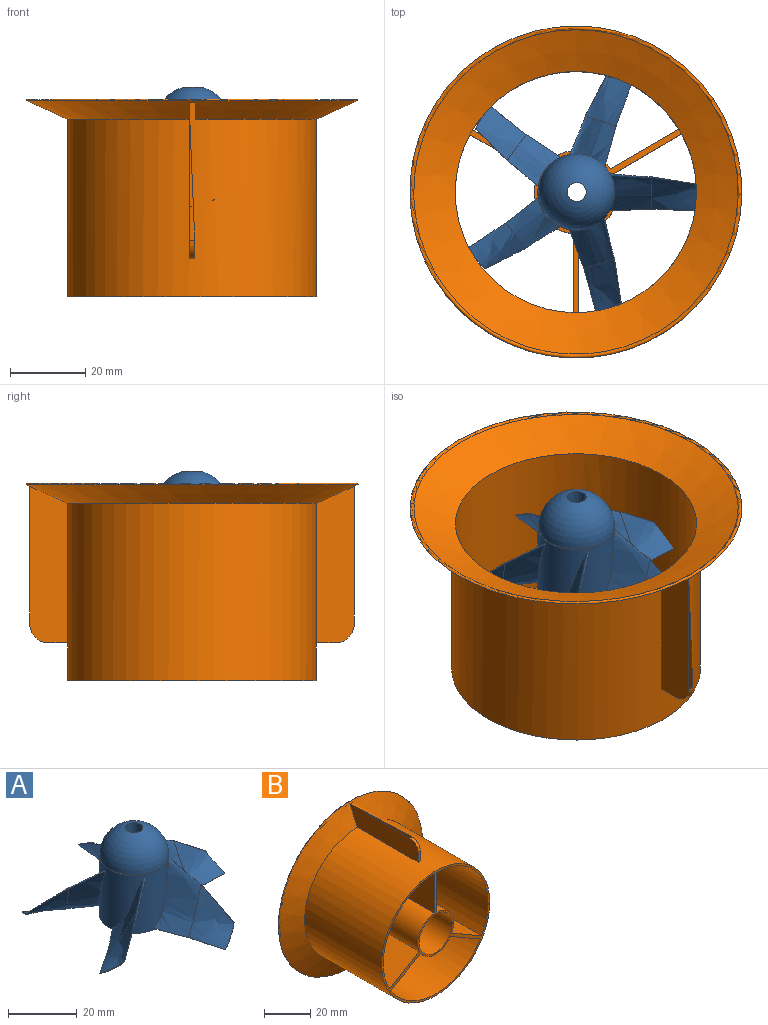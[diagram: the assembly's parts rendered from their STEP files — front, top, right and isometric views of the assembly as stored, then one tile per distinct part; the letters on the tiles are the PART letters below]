
ASSEMBLY  parts=2 mates=1
PART A: 38 faces, bbox 61.4x63.6x30.5 mm
  f0: bspline ~19.39x13.51mm, area 431mm2, adj f1,f36
  f1: cylinder r=10.1mm len=20.7mm, axis (0,0,-1), area 1234.5mm2, adj f0,f2,f5,f8,f11,f31,f32,f33
  f2: bspline ~19.22x14.14mm, area 417.3mm2, adj f1,f3
  f3: bspline ~14.62x13.87mm, area 306mm2, adj f2,f4
  f4: cylinder r=32mm len=6.27mm, axis (0,0,-1), area 2.2mm2, adj f3
  f5: bspline ~19.13x14.23mm, area 410.5mm2, adj f1,f6
  f6: bspline ~15.36x13.41mm, area 306mm2, adj f5,f7
  f7: cylinder r=32mm len=5.31mm, axis (0,0,-1), area 2.2mm2, adj f6
  f8: bspline ~19.4x11.33mm, area 432.5mm2, adj f1,f9
  f9: bspline ~13.41x12.41mm, area 306mm2, adj f8,f10
  f10: cylinder r=32mm len=7.16mm, axis (0,0,-1), area 2.2mm2, adj f9
  f11: plane 20.2x20.2mm, normal (0,0,-1), area 60.3mm2, adj f1,f12
  f12: cylinder r=9.1mm len=20.7mm, axis (0,0,-1), area 1183.5mm2, adj f11,f13,f14,f15,f16,f18,f19,f21
  f13: plane 0.06x0.02mm, normal (-1,0,0), area 0mm2, adj f12,f14,f15
  f14: bspline ~12.5x0.96mm, area 0mm2, adj f12,f13,f15
  f15: plane 0.06x0.04mm, normal (0,0,1), area 0mm2, adj f12,f13,f14
  f16: plane 0.32x0.21mm, normal (0,0,1), area 0mm2, adj f12,f17,f18
  f17: plane 0.1x0.03mm, normal (-0.31,0.95,0), area 0mm2, adj f16,f18
  f18: bspline ~0.35x0.21mm, area 0mm2, adj f12,f16,f17
  f19: plane 0.37x0.25mm, normal (0,0,1), area 0mm2, adj f12,f20,f21
  f20: plane 0.08x0.06mm, normal (0.81,-0.59,0), area 0mm2, adj f19,f21
  f21: bspline ~0.37x0.29mm, area 0mm2, adj f12,f19,f20
  f22: bspline ~0.49x0.42mm, area 0.1mm2, adj f12,f23,f24
  f23: plane 0.08x0.06mm, normal (0.81,0.59,0), area 0mm2, adj f22,f24
  f24: plane 0.44x0.42mm, normal (0,0,1), area 0.1mm2, adj f12,f22,f23
  f25: plane 0.08x0.03mm, normal (-0.31,-0.95,0), area 0mm2, adj f12,f26,f27
  f26: bspline ~12.19x3.98mm, area 0mm2, adj f12,f25,f27
  f27: plane 0.08x0.08mm, normal (0,0,1), area 0mm2, adj f12,f25,f26
  f28: plane 18.2x18.2mm, normal (0,0,-1), area 240.5mm2, adj f12,f29
  f29: cylinder r=2.5mm len=9.79mm, axis (0,0,-1), area 153.7mm2, adj f28,f30
  f30: sphere r=10.1mm, area 621mm2, adj f29,f31,f32
  f31: plane 20.2x10.21mm, normal (0,0,-1), area 4.6mm2, adj f1,f30
  f32: plane 20.2x10.21mm, normal (0,0,1), area 4.6mm2, adj f1,f30
  f33: bspline ~19.34x13.62mm, area 17.7mm2, adj f1,f34
  f34: bspline ~14.6x13.41mm, area 306mm2, adj f33,f35
  f35: cylinder r=32mm len=6.55mm, axis (0,0,-1), area 2.2mm2, adj f34
  f36: bspline ~13.82x13.41mm, area 306mm2, adj f0,f37
  f37: cylinder r=32mm len=7.06mm, axis (0,0,-1), area 2.2mm2, adj f36
PART B: 27 faces, bbox 95.3x52.4x95.3 mm
  f0: cylinder r=32mm len=64mm, axis (0,-1,0), area 9343.6mm2, adj f7,f8,f16,f17,f19,f20,f22,f23
  f1: plane 41.54x10.02mm, normal (-1,0,0), area 387.9mm2, adj f2,f5,f6,f10,f15
  f2: cylinder r=43mm len=36.54mm, axis (0,-1,0), area 54.8mm2, adj f1,f3,f5,f15
  f3: plane 41.54x10.02mm, normal (1,0,0), area 387.9mm2, adj f2,f5,f6,f10,f15
  f4: cylinder r=43mm len=36.55mm, axis (0,-1,0), area 54.8mm2, adj f5,f11,f12,f14
  f5: cone r=33mm half-angle=65.6deg, axis (0,1,0), area 2896.4mm2, adj f1,f2,f3,f4,f6,f9,f11,f12
  f6: cylinder r=33mm len=66mm, axis (0,-1,0), area 9634.2mm2, adj f1,f3,f5,f7,f10,f11,f12,f13
  f7: plane 66x66mm, normal (0,-1,0), area 360.1mm2, adj f0,f6,f16,f17,f18,f19,f20,f21
  f8: cone r=31.99mm half-angle=65.6deg, axis (0,1,0), area 2852.7mm2, adj f0,f9
  f9: torus R=43.52mm, axis (0,-1,0), area 371.9mm2, adj f5,f8
  f10: plane 5.02x1.5mm, normal (0,-1,0), area 7.5mm2, adj f1,f3,f6,f15
  f11: plane 41.54x10.02mm, normal (-1,0,0), area 388mm2, adj f4,f5,f6,f13,f14
  f12: plane 41.54x10.02mm, normal (1,0,0), area 388mm2, adj f4,f5,f6,f13,f14
  f13: plane 5.2x1.5mm, normal (0,-1,0), area 7.8mm2, adj f6,f11,f12,f14
  f14: cylinder r=5mm len=5mm, axis (1,0,0), area 11.5mm2, adj f4,f11,f12,f13
  f15: cylinder r=5mm len=5mm, axis (1,0,0), area 11.8mm2, adj f1,f2,f3,f10
  f16: plane 24x18.2mm, normal (-0.5,0,0.87), area 504.5mm2, adj f0,f7,f24,f26
  f17: plane 24x18.25mm, normal (0.5,0,-0.87), area 504.5mm2, adj f0,f7,f18,f26
  f18: cylinder r=11mm len=24mm, axis (0,-1,0), area 515mm2, adj f7,f17,f19,f26
  f19: plane 24x18.2mm, normal (-0.5,0,-0.87), area 504.5mm2, adj f0,f7,f18,f26
  f20: plane 24x18.15mm, normal (0.5,0,0.86), area 504.5mm2, adj f0,f7,f21,f26
  f21: cylinder r=11mm len=24mm, axis (0,-1,0), area 515mm2, adj f7,f20,f22,f26
  f22: plane 24x21.02mm, normal (1,0,0), area 504.5mm2, adj f0,f7,f21,f26
  f23: plane 24x21.02mm, normal (-1,0,0), area 504.5mm2, adj f0,f7,f24,f26
  f24: cylinder r=11mm len=24mm, axis (0,-1,0), area 515mm2, adj f7,f16,f23,f26
  f25: cylinder r=10.1mm len=24mm, axis (0,-1,0), area 1523mm2, adj f7,f26
  f26: plane 56.15x48.71mm, normal (0,1,0), area 155.9mm2, adj f0,f16,f17,f18,f19,f20,f21,f22
PLACE A t=(-56.24,-43.4,-37.01)mm
PLACE B rot(axis=(1,0,0),90deg) t=(-63.87,-38.4,-62.51)mm
MATE cylindrical B.f0 <-> A.f1  axis (0,0,-1) through (-63.87,-38.4,-38.51)mm
